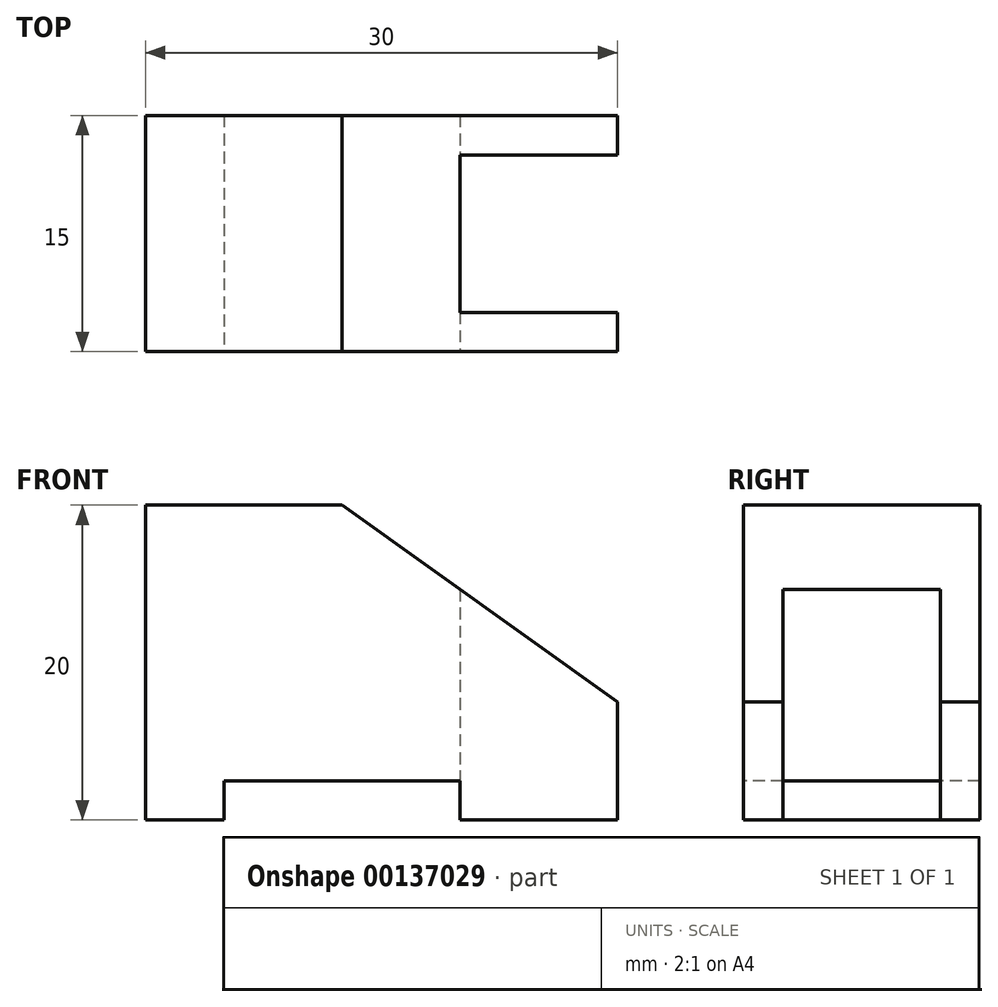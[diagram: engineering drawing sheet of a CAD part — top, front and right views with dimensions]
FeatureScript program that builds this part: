
annotation { "Feature Type Name" : "Feature", "Feature Type Description" : "" }
export const myFeature = defineFeature(function(context is Context, id is Id, definition is map)
    precondition{}
    {
        {
            var Q0;
            Q0=qCreatedBy(makeId("Front.planeOp"),FACE);
            var sketch = newSketch(context, id + "F0", { "sketchPlane" : qUnion([Q0])});
            skLineSegment(sketch, "E0.bottom", {"start": v(0, 0) * mm, "end": v(30, 0) * mm, "construction": true});
            skLineSegment(sketch, "E0.top", {"start": v(0, 20) * mm, "end": v(30, 20) * mm, "construction": true});
            skLineSegment(sketch, "E0.left", {"start": v(0, 0) * mm, "end": v(0, 20) * mm, "construction": true});
            skLineSegment(sketch, "E0.right", {"start": v(30, 0) * mm, "end": v(30, 20) * mm, "construction": true});
            skLineSegment(sketch, "E1", {"start": v(0, 20) * mm, "end": v(0, 0) * mm});
            skLineSegment(sketch, "E2", {"start": v(0, 20) * mm, "end": v(12.5, 20) * mm});
            skLineSegment(sketch, "E3", {"start": v(12.5, 20) * mm, "end": v(30, 7.5) * mm});
            skLineSegment(sketch, "E4", {"start": v(30, 7.5) * mm, "end": v(30, 0) * mm});
            skLineSegment(sketch, "E5", {"start": v(30, 0) * mm, "end": v(20, 0) * mm});
            skLineSegment(sketch, "E6", {"start": v(20, 0) * mm, "end": v(20, 2.5) * mm});
            skLineSegment(sketch, "E7", {"start": v(20, 2.5) * mm, "end": v(5, 2.5) * mm});
            skLineSegment(sketch, "E8", {"start": v(5, 2.5) * mm, "end": v(5, 0) * mm});
            skLineSegment(sketch, "E9", {"start": v(5, 0) * mm, "end": v(0, 0) * mm});
            skSolve(sketch);
        }
        {
            var Q0;
            Q0 = qSketchRegion(id + "F0", true);
            extrude(context, id + "F1", {"entities" : qUnion([Q0]), "oppositeDirection" : true, "depth" : 15 * mm});
        }
        {
            var Q0;
            Q0=makeQuery(id+"F1.opExtrude","SWEPT_FACE",FACE,{"disambiguationData":[OSD([sQuery(id+"F0.wireOp",EDGE,"E5")])]});
            var sketch = newSketch(context, id + "F2", { "sketchPlane" : qUnion([Q0])});
            skLineSegment(sketch, "E10.bottom", {"start": v(30, -2.5) * mm, "end": v(20, -2.5) * mm});
            skLineSegment(sketch, "E10.top", {"start": v(30, -12.5) * mm, "end": v(20, -12.5) * mm});
            skLineSegment(sketch, "E10.left", {"start": v(30, -2.5) * mm, "end": v(30, -12.5) * mm});
            skLineSegment(sketch, "E10.right", {"start": v(20, -2.5) * mm, "end": v(20, -12.5) * mm});
            skSolve(sketch);
        }
        {
            var Q0;
            Q0=makeQuery(id+"F2.imprint","IMPRINT",FACE,{"disambiguationData":[TD([[makeQuery(id+"F2.imprint","IMPRINT",EDGE,{"derivedFrom":sQuery(id+"F2.wireOp",EDGE,"E10.bottom")}),1.0]])]});
            extrude(context, id + "F3", {"entities" : qUnion([Q0]), "operationType" : NewBodyOperationType.REMOVE, "endBound" : BoundingType.THROUGH_ALL, "oppositeDirection" : true, "depth" : 25 * mm});
        }
    });
